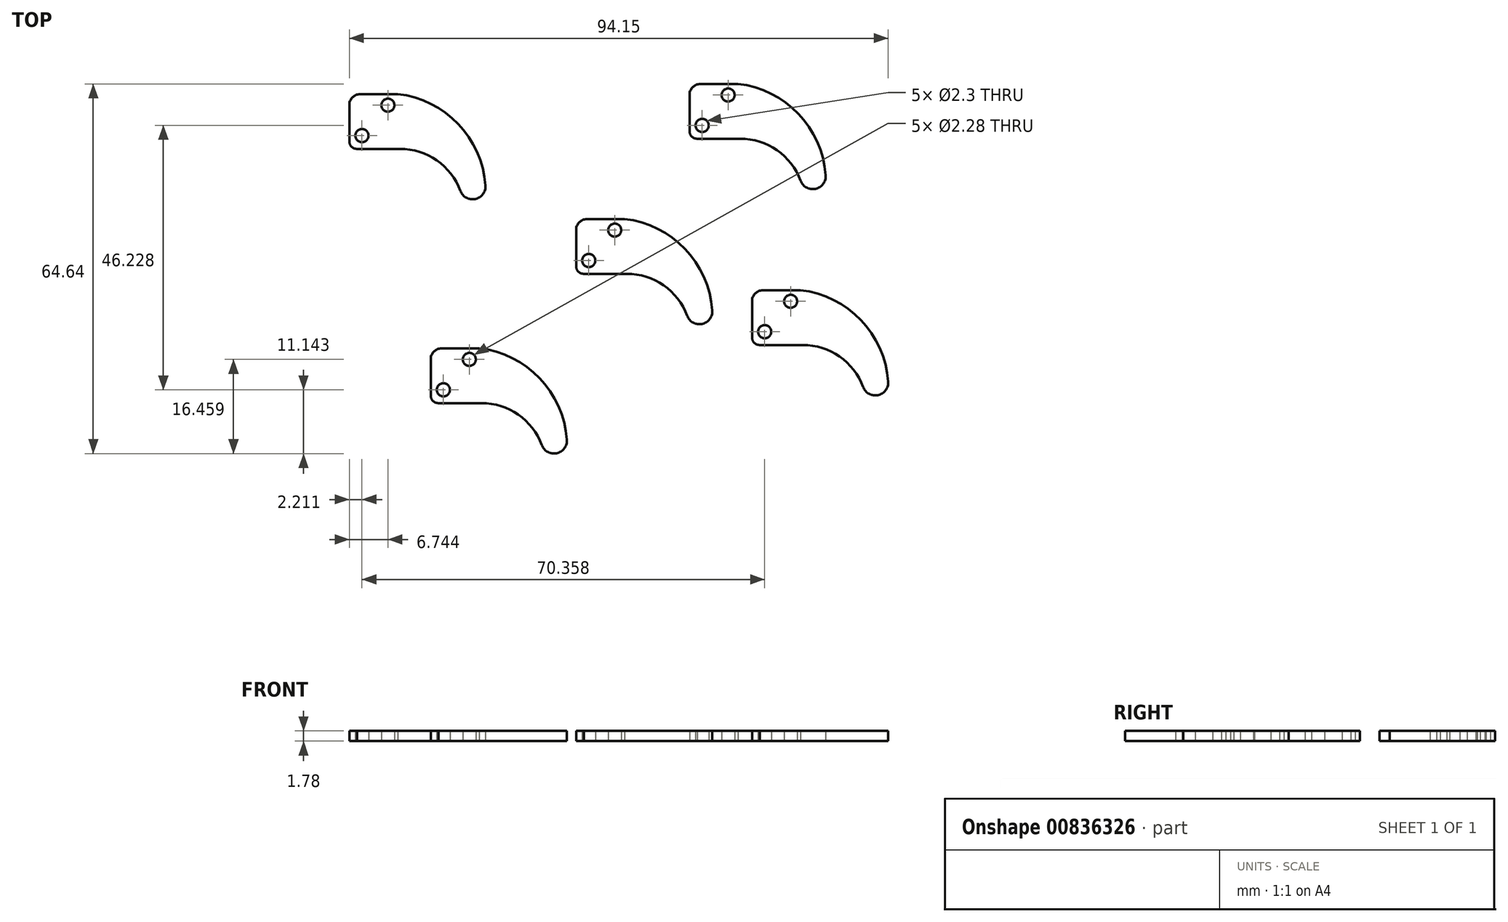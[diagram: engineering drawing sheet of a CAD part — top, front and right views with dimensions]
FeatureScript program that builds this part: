
annotation { "Feature Type Name" : "Feature", "Feature Type Description" : "" }
export const myFeature = defineFeature(function(context is Context, id is Id, definition is map)
    precondition{}
    {
        {
            var Q0;
            Q0=qCreatedBy(makeId("Top.planeOp"),FACE);
            var sketch = newSketch(context, id + "F0", { "sketchPlane" : qUnion([Q0])});
            skArc(sketch, "E0", {"start": v(-3.13, -1.89) * mm, "mid": v(-3, -3.54) * mm, "end": v(-1.35, -3.35) * mm});
            skArc(sketch, "E1", {"start": v(3.14, 1.92) * mm, "mid": v(3.02, 3.54) * mm, "end": v(1.4, 3.41) * mm});
            skLineSegment(sketch, "E2", {"start": v(-3.15, -1.92) * mm, "end": v(-3.13, -1.89) * mm});
            skLineSegment(sketch, "E3", {"start": v(-1.43, -3.45) * mm, "end": v(-1.35, -3.35) * mm});
            skCircle(sketch, "E4", {"center": v(2.27, 2.66) * mm, "radius": 1.14 * mm});
            skCircle(sketch, "E5", {"center": v(-2.26, -2.65) * mm, "radius": 1.15 * mm});
            skSolve(sketch);
        }
        {
            var Q0;
            Q0=qCreatedBy(makeId("Top.planeOp"),FACE);
            var sketch = newSketch(context, id + "F1", { "sketchPlane" : qUnion([Q0])});
            skLineSegment(sketch, "E6", {"start": v(3.98, 4.62) * mm, "end": v(-2.48, 4.62) * mm});
            skArc(sketch, "E7", {"start": v(-2.48, 4.62) * mm, "mid": v(-3.75, 4.17) * mm, "end": v(-4.47, 3.03) * mm});
            skLineSegment(sketch, "E8", {"start": v(-4.47, 3.03) * mm, "end": v(-4.47, -3.66) * mm});
            skArc(sketch, "E9", {"start": v(-4.47, -3.66) * mm, "mid": v(-4.06, -4.61) * mm, "end": v(-3.1, -4.97) * mm});
            skLineSegment(sketch, "E10", {"start": v(-3.1, -4.97) * mm, "end": v(4.38, -4.97) * mm});
            skArc(sketch, "E11", {"start": v(4.38, -4.97) * mm, "mid": v(10.81, -6.99) * mm, "end": v(14.94, -12.32) * mm});
            skArc(sketch, "E12", {"start": v(14.94, -12.32) * mm, "mid": v(17.54, -13.74) * mm, "end": v(19.31, -11.37) * mm});
            skArc(sketch, "E13", {"start": v(19.31, -11.37) * mm, "mid": v(14.54, -0.6) * mm, "end": v(3.98, 4.62) * mm});
            skSolve(sketch);
        }
        {
            var Q0;
            Q0 = qSketchRegion(id + "F1", true);
            extrude(context, id + "F2", {"entities" : qUnion([Q0]), "depth" : 1.78 * mm, "offsetDistance" : 25.4 * mm});
        }
        {
            var Q0;
            Q0 = qSketchRegion(id + "F0", true);
            extrude(context, id + "F3", {"entities" : qUnion([Q0]), "operationType" : NewBodyOperationType.REMOVE, "endBound" : BoundingType.UP_TO_NEXT, "depth" : 25.4 * mm, "offsetDistance" : 25.4 * mm});
        }
        {
            var Q0;
            Q0=makeQuery(id+"F2.opExtrude","SWEPT_BODY",BODY,{"disambiguationData":[OSD([sQuery(id+"F1.wireOp",EDGE,"E6"),sQuery(id+"F1.wireOp",EDGE,"E7"),sQuery(id+"F1.wireOp",EDGE,"E8"),sQuery(id+"F1.wireOp",EDGE,"E9"),sQuery(id+"F1.wireOp",EDGE,"E10"),sQuery(id+"F1.wireOp",EDGE,"E11"),sQuery(id+"F1.wireOp",EDGE,"E12"),sQuery(id+"F1.wireOp",EDGE,"E13")])]});
            transform(context, id + "F4", {"entities" : qUnion([Q0]), "transformType" : TransformType.TRANSLATION_3D, "dx" : 23.37 * mm, "dy" : 0 * mm, "dz" : 0 * mm, "makeCopy" : true});
        }
        {
            var Q0;
            Q0=makeQuery(id+"F2.opExtrude","SWEPT_BODY",BODY,{"disambiguationData":[OSD([sQuery(id+"F1.wireOp",EDGE,"E6"),sQuery(id+"F1.wireOp",EDGE,"E7"),sQuery(id+"F1.wireOp",EDGE,"E8"),sQuery(id+"F1.wireOp",EDGE,"E9"),sQuery(id+"F1.wireOp",EDGE,"E10"),sQuery(id+"F1.wireOp",EDGE,"E11"),sQuery(id+"F1.wireOp",EDGE,"E12"),sQuery(id+"F1.wireOp",EDGE,"E13")])]});
            transform(context, id + "F5", {"entities" : qUnion([Q0]), "transformType" : TransformType.TRANSLATION_3D, "dx" : 0 * mm, "dy" : 22.35 * mm, "dz" : 0 * mm, "makeCopy" : true});
        }
        {
            var Q0;
            Q0=makeQuery(id+"F2.opExtrude","SWEPT_BODY",BODY,{"disambiguationData":[OSD([sQuery(id+"F1.wireOp",EDGE,"E6"),sQuery(id+"F1.wireOp",EDGE,"E7"),sQuery(id+"F1.wireOp",EDGE,"E8"),sQuery(id+"F1.wireOp",EDGE,"E9"),sQuery(id+"F1.wireOp",EDGE,"E10"),sQuery(id+"F1.wireOp",EDGE,"E11"),sQuery(id+"F1.wireOp",EDGE,"E12"),sQuery(id+"F1.wireOp",EDGE,"E13")])]});
            transform(context, id + "F6", {"entities" : qUnion([Q0]), "transformType" : TransformType.TRANSLATION_3D, "dx" : -27.7 * mm, "dy" : 0 * mm, "dz" : 0 * mm, "makeCopy" : true});
        }
        {
            var Q0;
            Q0=makeQuery(id+"F2.opExtrude","SWEPT_BODY",BODY,{"disambiguationData":[OSD([sQuery(id+"F1.wireOp",EDGE,"E6"),sQuery(id+"F1.wireOp",EDGE,"E7"),sQuery(id+"F1.wireOp",EDGE,"E8"),sQuery(id+"F1.wireOp",EDGE,"E9"),sQuery(id+"F1.wireOp",EDGE,"E10"),sQuery(id+"F1.wireOp",EDGE,"E11"),sQuery(id+"F1.wireOp",EDGE,"E12"),sQuery(id+"F1.wireOp",EDGE,"E13")])]});
            transform(context, id + "F7", {"entities" : qUnion([Q0]), "transformType" : TransformType.TRANSLATION_3D, "dx" : 0 * mm, "dy" : -28.45 * mm, "dz" : 0 * mm, "makeCopy" : true});
        }
        {
            var Q0;
            Q0=makeQuery(id+"F4.opPattern","COPY",BODY,{"derivedFrom":makeQuery(id+"F2.opExtrude","SWEPT_BODY",BODY,{"disambiguationData":[OSD([sQuery(id+"F1.wireOp",EDGE,"E6"),sQuery(id+"F1.wireOp",EDGE,"E7"),sQuery(id+"F1.wireOp",EDGE,"E8"),sQuery(id+"F1.wireOp",EDGE,"E9"),sQuery(id+"F1.wireOp",EDGE,"E10"),sQuery(id+"F1.wireOp",EDGE,"E11"),sQuery(id+"F1.wireOp",EDGE,"E12"),sQuery(id+"F1.wireOp",EDGE,"E13")])]}),"instanceName":"1"});
            var Q1;
            Q1=makeQuery(id+"F5.opPattern","COPY",BODY,{"derivedFrom":makeQuery(id+"F2.opExtrude","SWEPT_BODY",BODY,{"disambiguationData":[OSD([sQuery(id+"F1.wireOp",EDGE,"E6"),sQuery(id+"F1.wireOp",EDGE,"E7"),sQuery(id+"F1.wireOp",EDGE,"E8"),sQuery(id+"F1.wireOp",EDGE,"E9"),sQuery(id+"F1.wireOp",EDGE,"E10"),sQuery(id+"F1.wireOp",EDGE,"E11"),sQuery(id+"F1.wireOp",EDGE,"E12"),sQuery(id+"F1.wireOp",EDGE,"E13")])]}),"instanceName":"1"});
            var Q2;
            Q2=makeQuery(id+"F6.opPattern","COPY",BODY,{"derivedFrom":makeQuery(id+"F2.opExtrude","SWEPT_BODY",BODY,{"disambiguationData":[OSD([sQuery(id+"F1.wireOp",EDGE,"E6"),sQuery(id+"F1.wireOp",EDGE,"E7"),sQuery(id+"F1.wireOp",EDGE,"E8"),sQuery(id+"F1.wireOp",EDGE,"E9"),sQuery(id+"F1.wireOp",EDGE,"E10"),sQuery(id+"F1.wireOp",EDGE,"E11"),sQuery(id+"F1.wireOp",EDGE,"E12"),sQuery(id+"F1.wireOp",EDGE,"E13")])]}),"instanceName":"1"});
            var Q3;
            Q3=makeQuery(id+"F7.opPattern","COPY",BODY,{"derivedFrom":makeQuery(id+"F2.opExtrude","SWEPT_BODY",BODY,{"disambiguationData":[OSD([sQuery(id+"F1.wireOp",EDGE,"E6"),sQuery(id+"F1.wireOp",EDGE,"E7"),sQuery(id+"F1.wireOp",EDGE,"E8"),sQuery(id+"F1.wireOp",EDGE,"E9"),sQuery(id+"F1.wireOp",EDGE,"E10"),sQuery(id+"F1.wireOp",EDGE,"E11"),sQuery(id+"F1.wireOp",EDGE,"E12"),sQuery(id+"F1.wireOp",EDGE,"E13")])]}),"instanceName":"1"});
            deleteBodies(context, id + "F8", {"entities" : qUnion([Q0, Q1, Q2, Q3])});
        }
        {
            var Q0;
            Q0=makeQuery(id+"F2.opExtrude","SWEPT_BODY",BODY,{"disambiguationData":[OSD([sQuery(id+"F1.wireOp",EDGE,"E6"),sQuery(id+"F1.wireOp",EDGE,"E7"),sQuery(id+"F1.wireOp",EDGE,"E8"),sQuery(id+"F1.wireOp",EDGE,"E9"),sQuery(id+"F1.wireOp",EDGE,"E10"),sQuery(id+"F1.wireOp",EDGE,"E11"),sQuery(id+"F1.wireOp",EDGE,"E12"),sQuery(id+"F1.wireOp",EDGE,"E13")])]});
            transform(context, id + "F9", {"entities" : qUnion([Q0]), "transformType" : TransformType.TRANSLATION_3D, "dx" : 30.73 * mm, "dy" : -12.45 * mm, "dz" : 0 * mm, "makeCopy" : true});
        }
        {
            var Q0;
            Q0=makeQuery(id+"F2.opExtrude","SWEPT_BODY",BODY,{"disambiguationData":[OSD([sQuery(id+"F1.wireOp",EDGE,"E6"),sQuery(id+"F1.wireOp",EDGE,"E7"),sQuery(id+"F1.wireOp",EDGE,"E8"),sQuery(id+"F1.wireOp",EDGE,"E9"),sQuery(id+"F1.wireOp",EDGE,"E10"),sQuery(id+"F1.wireOp",EDGE,"E11"),sQuery(id+"F1.wireOp",EDGE,"E12"),sQuery(id+"F1.wireOp",EDGE,"E13")])]});
            transform(context, id + "F10", {"entities" : qUnion([Q0]), "transformType" : TransformType.TRANSLATION_3D, "dx" : 19.8 * mm, "dy" : 23.62 * mm, "dz" : 0 * mm, "makeCopy" : true});
        }
        {
            var Q0;
            Q0=makeQuery(id+"F2.opExtrude","SWEPT_BODY",BODY,{"disambiguationData":[OSD([sQuery(id+"F1.wireOp",EDGE,"E6"),sQuery(id+"F1.wireOp",EDGE,"E7"),sQuery(id+"F1.wireOp",EDGE,"E8"),sQuery(id+"F1.wireOp",EDGE,"E9"),sQuery(id+"F1.wireOp",EDGE,"E10"),sQuery(id+"F1.wireOp",EDGE,"E11"),sQuery(id+"F1.wireOp",EDGE,"E12"),sQuery(id+"F1.wireOp",EDGE,"E13")])]});
            transform(context, id + "F11", {"entities" : qUnion([Q0]), "transformType" : TransformType.TRANSLATION_3D, "dx" : -39.62 * mm, "dy" : 21.84 * mm, "dz" : 0 * mm, "makeCopy" : true});
        }
        {
            var Q0;
            Q0=makeQuery(id+"F2.opExtrude","SWEPT_BODY",BODY,{"disambiguationData":[OSD([sQuery(id+"F1.wireOp",EDGE,"E6"),sQuery(id+"F1.wireOp",EDGE,"E7"),sQuery(id+"F1.wireOp",EDGE,"E8"),sQuery(id+"F1.wireOp",EDGE,"E9"),sQuery(id+"F1.wireOp",EDGE,"E10"),sQuery(id+"F1.wireOp",EDGE,"E11"),sQuery(id+"F1.wireOp",EDGE,"E12"),sQuery(id+"F1.wireOp",EDGE,"E13")])]});
            transform(context, id + "F12", {"entities" : qUnion([Q0]), "transformType" : TransformType.TRANSLATION_3D, "dx" : -25.4 * mm, "dy" : -22.6 * mm, "dz" : 0 * mm, "makeCopy" : true});
        }
    });
